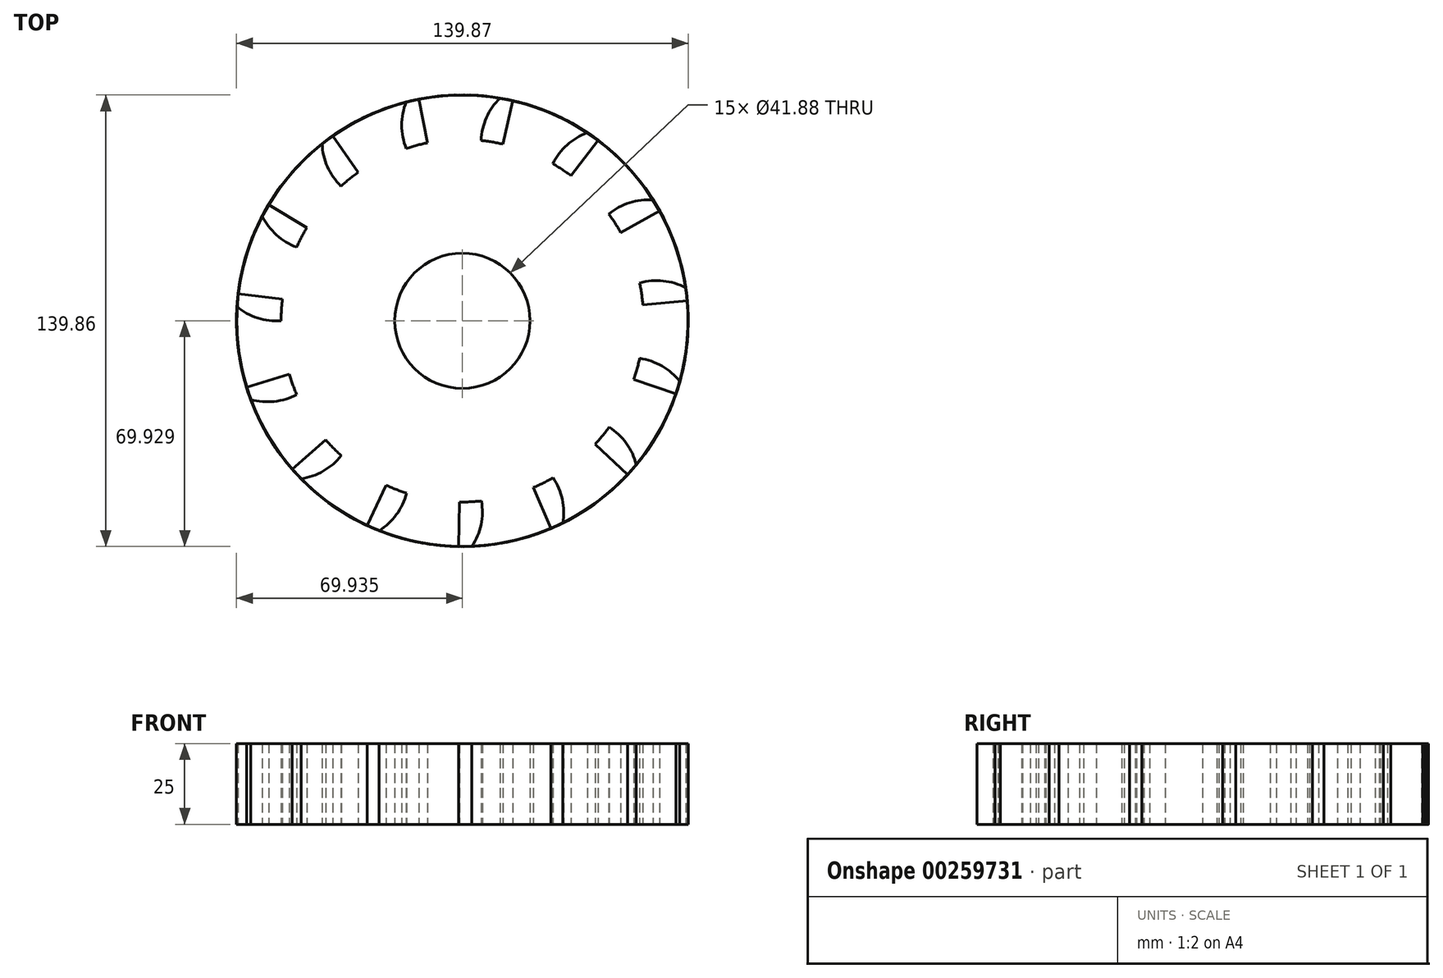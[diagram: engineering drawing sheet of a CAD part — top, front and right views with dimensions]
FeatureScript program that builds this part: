
annotation { "Feature Type Name" : "Feature", "Feature Type Description" : "" }
export const myFeature = defineFeature(function(context is Context, id is Id, definition is map)
    precondition{}
    {
        {
            var Q0;
            Q0=qCreatedBy(makeId("Top.planeOp"),FACE);
            var sketch = newSketch(context, id + "F0", { "sketchPlane" : qUnion([Q0])});
            skCircle(sketch, "E0", {"center": v(12.04, 33.45) * mm, "radius": 69.93 * mm});
            skCircle(sketch, "E1", {"center": v(12.04, 33.45) * mm, "radius": 56.13 * mm});
            skArc(sketch, "E2", {"start": v(-34.41, 1.95) * mm, "mid": v(-39.92, -2.87) * mm, "end": v(-43.22, -9.4) * mm});
            skLineSegment(sketch, "E3", {"start": v(12.04, 33.45) * mm, "end": v(-40.66, -12.51) * mm});
            skArc(sketch, "E4.MirrorCS", {"start": v(-25.48, -8.3) * mm, "mid": v(-31.01, -13.09) * mm, "end": v(-37.93, -15.47) * mm});
            skCircle(sketch, "E5", {"center": v(12.04, 33.45) * mm, "radius": 20.94 * mm});
            skSolve(sketch);
        }
        {
            var Q0;
            {var subQ3=sQuery(id+"F0.wireOp",EDGE,"E4.MirrorCS");Q0=makeQuery(id+"F0.imprint","IMPRINT",FACE,{"disambiguationData":[TD([[makeQuery(id+"F0.imprint","IMPRINT",EDGE,{"derivedFrom":subQ3}),-1.0]])]});}
            var Q1;
            {var subQ0=sQuery(id+"F0.wireOp",EDGE,"E1");var subQ1=makeQuery(id+"F0.imprint","INTERSECT",VERTEX,{"derivedFrom":[subQ0,sQuery(id+"F0.wireOp",EDGE,"E2")]});Q1=makeQuery(id+"F0.imprint","IMPRINT",FACE,{"disambiguationData":[TD([[makeQuery(id+"F0.imprint","IMPRINT",EDGE,{"disambiguationData":[TD([[subQ1,-1.0]])],"derivedFrom":subQ0}),1.0]])]});}
            var Q2;
            {var subQ0=sQuery(id+"F0.wireOp",EDGE,"E2");Q2=makeQuery(id+"F0.imprint","IMPRINT",FACE,{"disambiguationData":[TD([[makeQuery(id+"F0.imprint","IMPRINT",EDGE,{"derivedFrom":subQ0}),1.0]])]});}
            extrude(context, id + "F1", {"entities" : qUnion([Q0, Q1, Q2]), "depth" : 25 * mm});
        }
        {
            var Q0;
            Q0=makeQuery(id+"F1.opExtrude","SWEPT_BODY",BODY,{"disambiguationData":[OSD([sQuery(id+"F0.wireOp",EDGE,"E0"),sQuery(id+"F0.wireOp",EDGE,"E1"),sQuery(id+"F0.wireOp",EDGE,"E2"),sQuery(id+"F0.wireOp",EDGE,"E4.MirrorCS"),sQuery(id+"F0.wireOp",EDGE,"E5")])]});
            var Q1;
            Q1=makeQuery(id+"F1.opExtrude","SWEPT_FACE",FACE,{"disambiguationData":[OSD([sQuery(id+"F0.wireOp",EDGE,"E5")])]});
            circularPattern(context, id + "F2", {"entities" : qUnion([Q0]), "axis" : qUnion([Q1]), "angle" : 360 * degree, "instanceCount" : 15, "equalSpace" : true});
        }
    });
